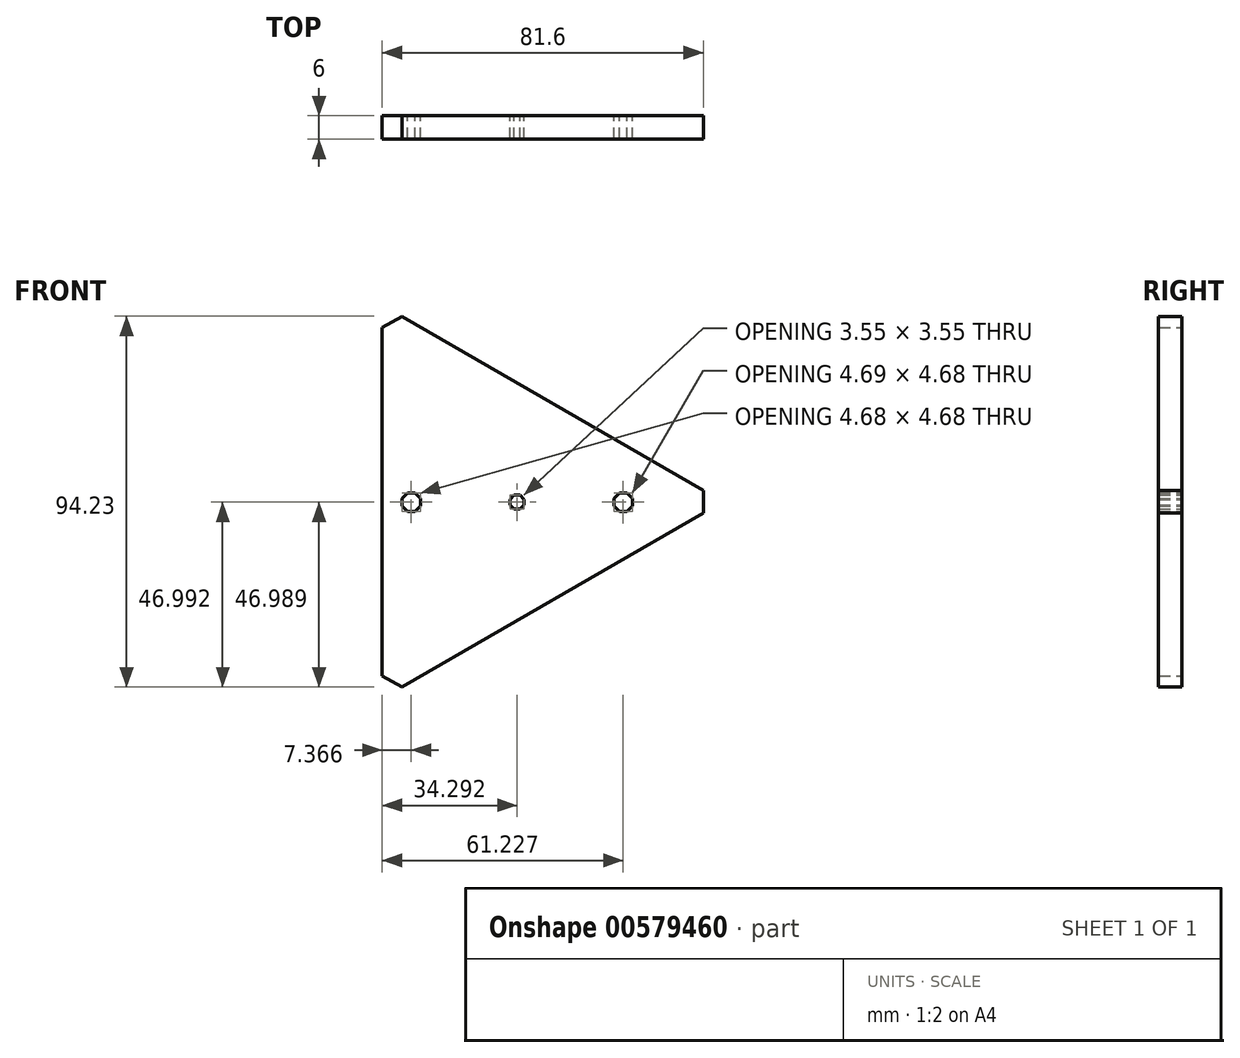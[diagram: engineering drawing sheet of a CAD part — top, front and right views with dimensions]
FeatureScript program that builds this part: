
annotation { "Feature Type Name" : "Feature", "Feature Type Description" : "" }
export const myFeature = defineFeature(function(context is Context, id is Id, definition is map)
    precondition{}
    {
        {
            var Q0;
            Q0=qCreatedBy(makeId("Front.planeOp"),FACE);
            var sketch = newSketch(context, id + "F0", { "sketchPlane" : qUnion([Q0])});
            skLineSegment(sketch, "E0", {"start": v(-43.7, 0.05) * mm, "end": v(-42.32, 1.42) * mm});
            skLineSegment(sketch, "E1", {"start": v(-42.32, 1.42) * mm, "end": v(-40.39, 1.42) * mm});
            skLineSegment(sketch, "E2", {"start": v(-40.39, 1.42) * mm, "end": v(-39.02, 0.05) * mm});
            skLineSegment(sketch, "E3", {"start": v(-39.02, 0.05) * mm, "end": v(-39.02, -1.89) * mm});
            skLineSegment(sketch, "E4", {"start": v(-39.02, -1.89) * mm, "end": v(-40.39, -3.26) * mm});
            skLineSegment(sketch, "E5", {"start": v(-40.39, -3.26) * mm, "end": v(-42.32, -3.26) * mm});
            skLineSegment(sketch, "E6", {"start": v(-42.32, -3.26) * mm, "end": v(-43.7, -1.89) * mm});
            skLineSegment(sketch, "E7", {"start": v(-43.7, -1.89) * mm, "end": v(-43.7, 0.05) * mm});
            skLineSegment(sketch, "E8", {"start": v(-16.2, -0.18) * mm, "end": v(-16.2, -1.65) * mm});
            skLineSegment(sketch, "E9", {"start": v(-16.2, -1.65) * mm, "end": v(-15.17, -2.7) * mm});
            skLineSegment(sketch, "E10", {"start": v(-15.17, -2.7) * mm, "end": v(-13.7, -2.7) * mm});
            skLineSegment(sketch, "E11", {"start": v(-13.7, -2.7) * mm, "end": v(-12.65, -1.65) * mm});
            skLineSegment(sketch, "E12", {"start": v(-12.65, -1.65) * mm, "end": v(-12.65, -0.18) * mm});
            skLineSegment(sketch, "E13", {"start": v(-12.65, -0.18) * mm, "end": v(-13.7, 0.86) * mm});
            skLineSegment(sketch, "E14", {"start": v(-13.7, 0.86) * mm, "end": v(-15.16, 0.86) * mm});
            skLineSegment(sketch, "E15", {"start": v(-15.16, 0.86) * mm, "end": v(-16.2, -0.18) * mm});
            skLineSegment(sketch, "E16", {"start": v(11.53, 1.42) * mm, "end": v(10.16, 0.05) * mm});
            skLineSegment(sketch, "E17", {"start": v(10.16, 0.05) * mm, "end": v(10.16, -1.89) * mm});
            skLineSegment(sketch, "E18", {"start": v(10.16, -1.89) * mm, "end": v(11.53, -3.26) * mm});
            skLineSegment(sketch, "E19", {"start": v(11.53, -3.26) * mm, "end": v(13.49, -3.26) * mm});
            skLineSegment(sketch, "E20", {"start": v(13.49, -3.26) * mm, "end": v(14.85, -1.9) * mm});
            skLineSegment(sketch, "E21", {"start": v(14.85, -1.9) * mm, "end": v(14.85, 0.05) * mm});
            skLineSegment(sketch, "E22", {"start": v(14.85, 0.05) * mm, "end": v(13.52, 1.39) * mm});
            skLineSegment(sketch, "E23", {"start": v(13.52, 1.39) * mm, "end": v(11.53, 1.42) * mm});
            skLineSegment(sketch, "E24", {"start": v(-43.72, -47.91) * mm, "end": v(32.88, -3.68) * mm});
            skLineSegment(sketch, "E25", {"start": v(32.88, 2.09) * mm, "end": v(-43.72, 46.32) * mm});
            skLineSegment(sketch, "E26", {"start": v(-48.72, 43.43) * mm, "end": v(-48.72, -45.02) * mm});
            skLineSegment(sketch, "E27", {"start": v(-48.72, 43.43) * mm, "end": v(-43.72, 46.32) * mm});
            skLineSegment(sketch, "E28", {"start": v(-48.72, -45.02) * mm, "end": v(-43.72, -47.91) * mm});
            skLineSegment(sketch, "E29", {"start": v(32.88, 2.09) * mm, "end": v(32.88, -3.68) * mm});
            skPoint(sketch, "E30.endSnap0", {"position": v(32.88, -0.8) * mm});
            skPoint(sketch, "E31.start.orphan", {"position": v(-46.22, -46.47) * mm});
            skPoint(sketch, "E30.end.orphan", {"position": v(32.88, -0.8) * mm});
            skPoint(sketch, "E32.end.orphan", {"position": v(-46.22, 44.87) * mm});
            skSolve(sketch);
        }
        {
            var Q0;
            Q0 = qSketchRegion(id + "F0", true);
            extrude(context, id + "F1", {"entities" : qUnion([Q0]), "depth" : 6 * mm, "offsetDistance" : 25 * mm});
        }
        {
            var Q0;
            Q0=makeQuery(id+"F1.opExtrude","SWEPT_FACE",FACE,{"disambiguationData":[OSD([sQuery(id+"F0.wireOp",EDGE,"E28")])]});
            cPlane(context, id + "F2", {"entities" : qUnion([Q0]), "cplaneType" : CPlaneType.OFFSET, "offset" : 0 * mm, "width" : 150 * mm, "height" : 150 * mm});
        }
    });
